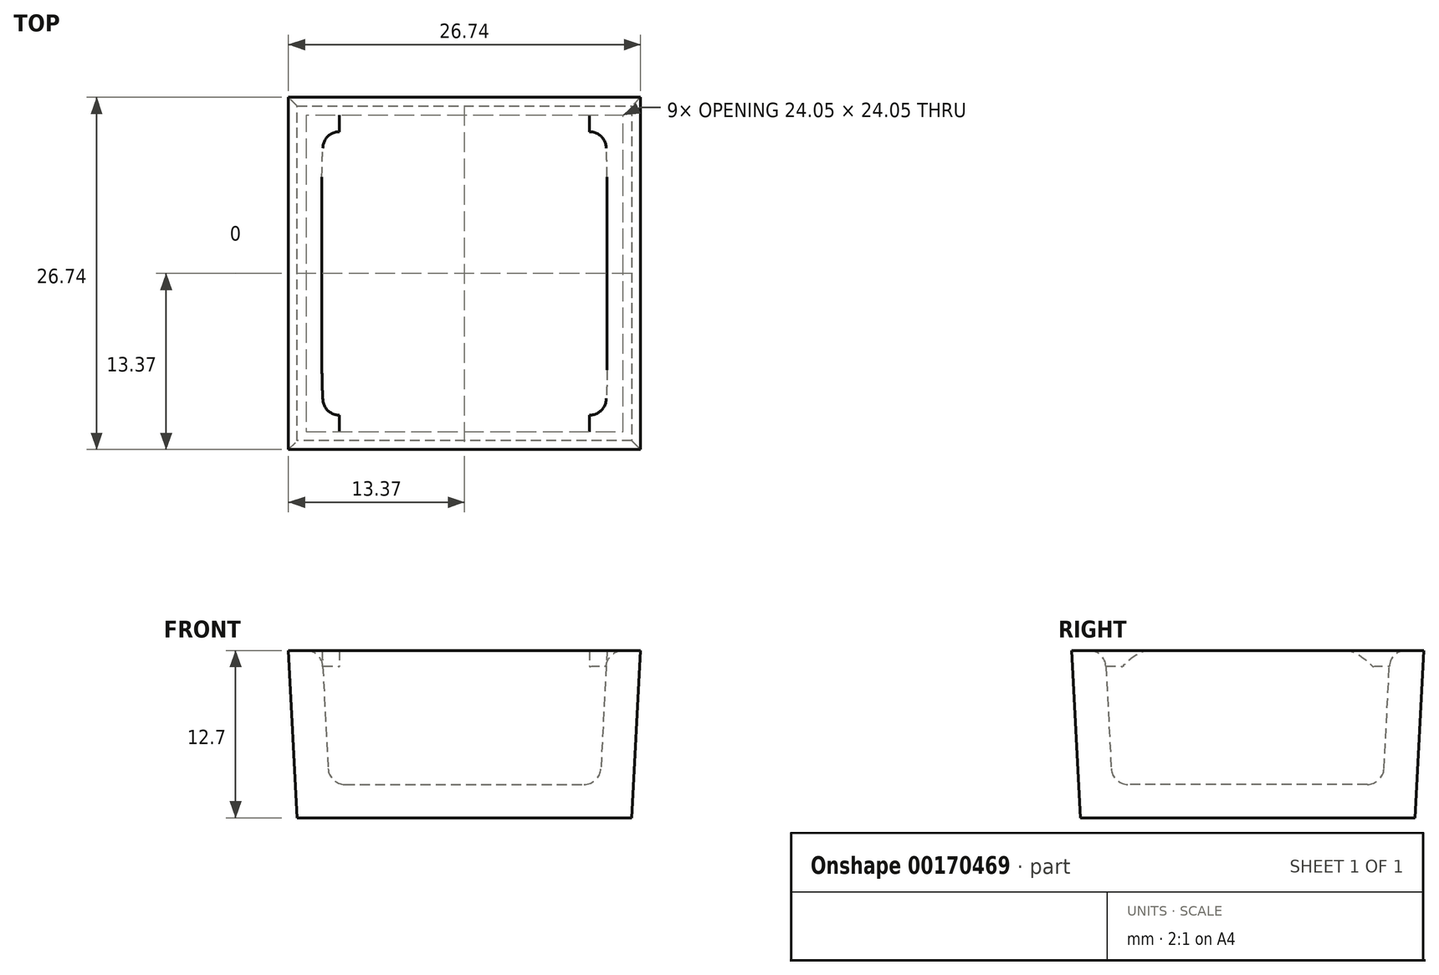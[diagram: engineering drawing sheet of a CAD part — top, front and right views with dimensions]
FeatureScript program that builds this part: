
annotation { "Feature Type Name" : "Feature", "Feature Type Description" : "" }
export const myFeature = defineFeature(function(context is Context, id is Id, definition is map)
    precondition{}
    {
        {
            var Q0;
            Q0=qCreatedBy(makeId("Top.planeOp"),FACE);
            var sketch = newSketch(context, id + "F0", { "sketchPlane" : qUnion([Q0])});
            skLineSegment(sketch, "E0.bottom", {"start": v(12.7, -12.7) * mm, "end": v(-12.7, -12.7) * mm});
            skLineSegment(sketch, "E0.top", {"start": v(12.7, 12.7) * mm, "end": v(-12.7, 12.7) * mm});
            skLineSegment(sketch, "E0.left", {"start": v(12.7, -12.7) * mm, "end": v(12.7, 12.7) * mm});
            skLineSegment(sketch, "E0.right", {"start": v(-12.7, -12.7) * mm, "end": v(-12.7, 12.7) * mm});
            skPoint(sketch, "E0.middle", {"position": v(0, 0) * mm});
            skSolve(sketch);
        }
        {
            var Q0;
            Q0=makeQuery(id+"F0.imprint","IMPRINT",FACE,{"disambiguationData":[TD([[makeQuery(id+"F0.imprint","IMPRINT",EDGE,{"derivedFrom":sQuery(id+"F0.wireOp",EDGE,"E0.bottom")}),-1.0]])]});
            extrude(context, id + "F1", {"entities" : qUnion([Q0]), "depth" : 12.7 * mm, "hasDraft" : true, "draftAngle" : 3 * degree});
        }
        {
            var Q0;
            Q0=makeQuery(id+"F1.opExtrude","CAP_FACE",FACE,{"disambiguationData":[OSD([sQuery(id+"F0.wireOp",EDGE,"E0.bottom"),sQuery(id+"F0.wireOp",EDGE,"E0.top"),sQuery(id+"F0.wireOp",EDGE,"E0.left"),sQuery(id+"F0.wireOp",EDGE,"E0.right")])],"isStart":false});
            shell(context, id + "F2", {"entities" : qUnion([Q0]), "thickness" : 2.54 * mm});
        }
        {
            var Q0;
            Q0=makeQuery(id+"F2.opShell","OFFSET_FACE",FACE,{"disambiguationData":[OSD([sQuery(id+"F0.wireOp",EDGE,"E0.bottom"),sQuery(id+"F0.wireOp",EDGE,"E0.top"),sQuery(id+"F0.wireOp",EDGE,"E0.left"),sQuery(id+"F0.wireOp",EDGE,"E0.right")])]});
            var Q1;
            Q1=makeQuery(id+"F2.opShell","OFFSET_EDGE",EDGE,{"disambiguationData":[OSD([sQuery(id+"F0.wireOp",EDGE,"E0.top"),sQuery(id+"F0.wireOp",EDGE,"E0.right")])]});
            var Q2;
            Q2=makeQuery(id+"F2.opShell","OFFSET_FACE",FACE,{"disambiguationData":[OSD([sQuery(id+"F0.wireOp",EDGE,"E0.top")])]});
            var Q3;
            Q3=makeQuery(id+"F2.opShell","OFFSET_FACE",FACE,{"disambiguationData":[OSD([sQuery(id+"F0.wireOp",EDGE,"E0.bottom")])]});
            fillet(context, id + "F3", {"entities" : qUnion([Q0, Q1, Q2, Q3]), "radius" : 1.27 * mm, "tangentPropagation" : true, "allowEdgeOverflow" : false});
        }
    });
